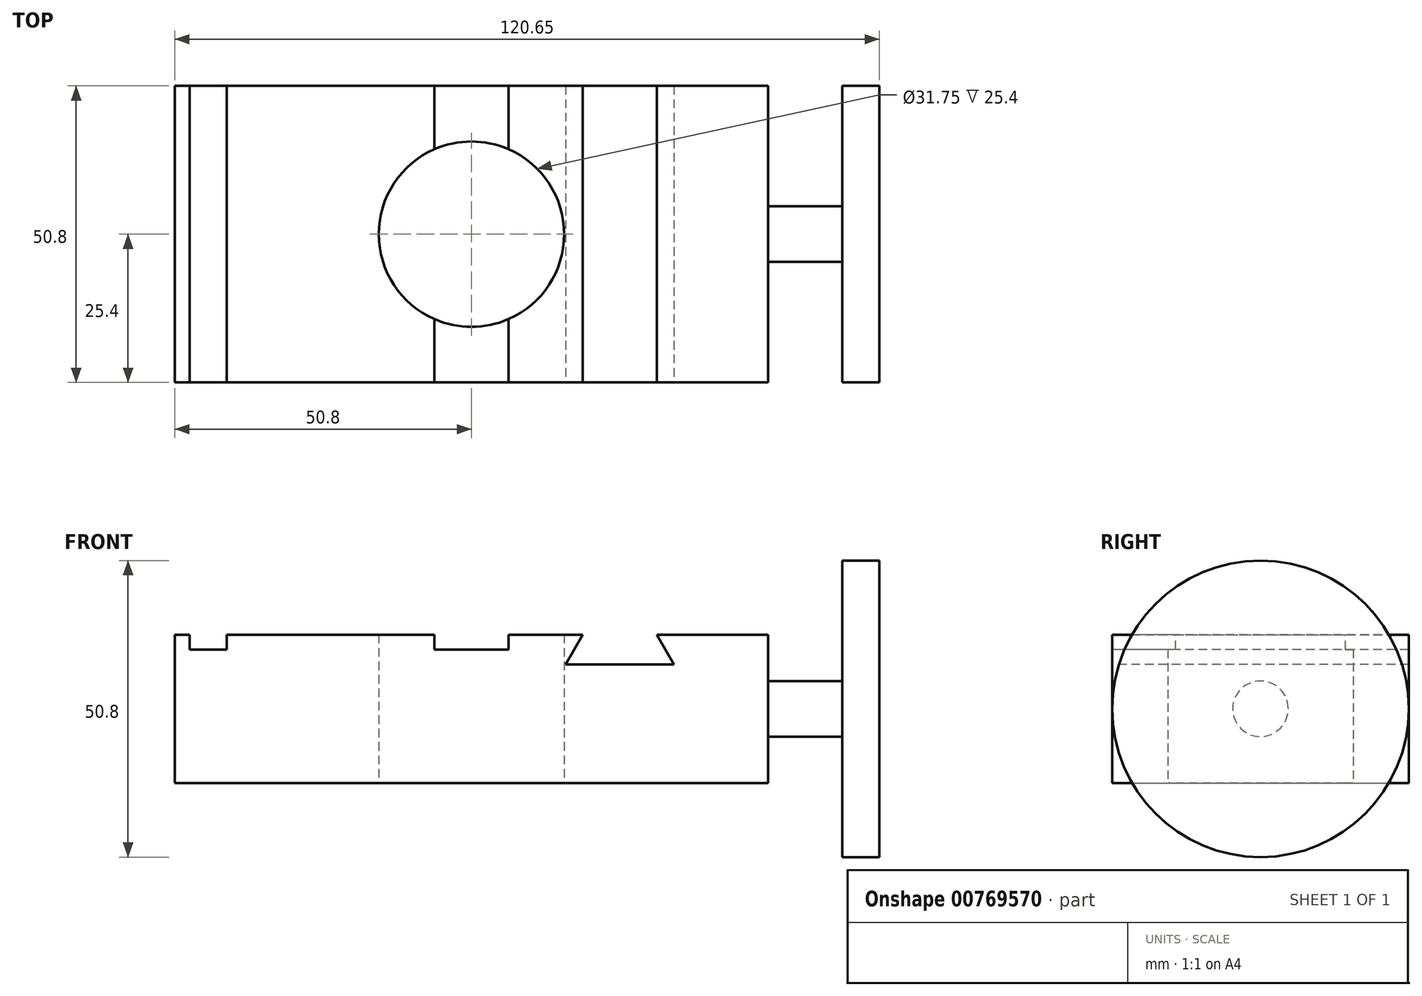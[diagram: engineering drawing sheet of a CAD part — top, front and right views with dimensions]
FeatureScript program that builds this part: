
annotation { "Feature Type Name" : "Feature", "Feature Type Description" : "" }
export const myFeature = defineFeature(function(context is Context, id is Id, definition is map)
    precondition{}
    {
        {
            var Q0;
            Q0=qCreatedBy(makeId("Top.planeOp"),FACE);
            var sketch = newSketch(context, id + "F0", { "sketchPlane" : qUnion([Q0])});
            skLineSegment(sketch, "E0.bottom", {"start": v(50.8, -25.4) * mm, "end": v(-50.8, -25.4) * mm});
            skLineSegment(sketch, "E0.top", {"start": v(50.8, 25.4) * mm, "end": v(-50.8, 25.4) * mm});
            skLineSegment(sketch, "E0.left", {"start": v(50.8, -25.4) * mm, "end": v(50.8, 25.4) * mm});
            skLineSegment(sketch, "E0.right", {"start": v(-50.8, -25.4) * mm, "end": v(-50.8, 25.4) * mm});
            skPoint(sketch, "E0.middle", {"position": v(0, 0) * mm});
            skCircle(sketch, "E1", {"center": v(0, 0) * mm, "radius": 15.88 * mm});
            skSolve(sketch);
        }
        {
            var Q0;
            Q0=makeQuery(id+"F0.imprint","IMPRINT",FACE,{"disambiguationData":[TD([[makeQuery(id+"F0.imprint","IMPRINT",EDGE,{"derivedFrom":sQuery(id+"F0.wireOp",EDGE,"E0.bottom")}),-1.0]])]});
            extrude(context, id + "F1", {"entities" : qUnion([Q0]), "depth" : 25.4 * mm, "offsetDistance" : 25.4 * mm});
        }
        {
            var Q0;
            Q0=makeQuery(id+"F1.opExtrude","CAP_FACE",FACE,{"disambiguationData":[OSD([sQuery(id+"F0.wireOp",EDGE,"E0.bottom"),sQuery(id+"F0.wireOp",EDGE,"E0.top"),sQuery(id+"F0.wireOp",EDGE,"E0.left"),sQuery(id+"F0.wireOp",EDGE,"E0.right"),sQuery(id+"F0.wireOp",EDGE,"E1")])],"isStart":false});
            var sketch = newSketch(context, id + "F2", { "sketchPlane" : qUnion([Q0])});
            skLineSegment(sketch, "E2.bottom", {"start": v(-48.26, 25.4) * mm, "end": v(-41.9, 25.4) * mm});
            skLineSegment(sketch, "E2.top", {"start": v(-48.26, -25.4) * mm, "end": v(-41.9, -25.4) * mm});
            skLineSegment(sketch, "E2.left", {"start": v(-48.26, 25.4) * mm, "end": v(-48.26, -25.4) * mm});
            skLineSegment(sketch, "E2.right", {"start": v(-41.9, 25.4) * mm, "end": v(-41.9, -25.4) * mm});
            skLineSegment(sketch, "E3", {"start": v(-6.35, 25.4) * mm, "end": v(-6.35, -25.4) * mm});
            skLineSegment(sketch, "E4", {"start": v(-6.35, -25.4) * mm, "end": v(6.35, -25.4) * mm});
            skLineSegment(sketch, "E5", {"start": v(6.35, -25.4) * mm, "end": v(6.35, 25.4) * mm});
            skLineSegment(sketch, "E6", {"start": v(6.35, 25.4) * mm, "end": v(-6.35, 25.4) * mm});
            skPoint(sketch, "E7", {"position": v(0, 0) * mm});
            skLineSegment(sketch, "E8", {"start": v(0, 25.4) * mm, "end": v(0, -25.4) * mm, "construction": true});
            skSolve(sketch);
        }
        {
            var Q0;
            {var subQ0=sQuery(id+"F2.wireOp",EDGE,"E6");Q0=makeQuery(id+"F2.imprint","IMPRINT",FACE,{"disambiguationData":[TD([[makeQuery(id+"F2.imprint","IMPRINT",EDGE,{"derivedFrom":subQ0}),1.0]])]});}
            var Q1;
            {var subQ0=sQuery(id+"F2.wireOp",EDGE,"E4");Q1=makeQuery(id+"F2.imprint","IMPRINT",FACE,{"disambiguationData":[TD([[makeQuery(id+"F2.imprint","IMPRINT",EDGE,{"derivedFrom":subQ0}),-1.0]])]});}
            var Q2;
            Q2=makeQuery(id+"F2.imprint","IMPRINT",FACE,{"disambiguationData":[TD([[makeQuery(id+"F2.imprint","IMPRINT",EDGE,{"derivedFrom":sQuery(id+"F2.wireOp",EDGE,"E2.bottom")}),1.0]])]});
            extrude(context, id + "F3", {"entities" : qUnion([Q0, Q1, Q2]), "operationType" : NewBodyOperationType.REMOVE, "oppositeDirection" : true, "depth" : 2.54 * mm, "offsetDistance" : 25.4 * mm});
        }
        {
            var Q0;
            Q0=makeQuery(id+"F1.opExtrude","SWEPT_FACE",FACE,{"disambiguationData":[OSD([sQuery(id+"F0.wireOp",EDGE,"E0.bottom")])]});
            var sketch = newSketch(context, id + "F4", { "sketchPlane" : qUnion([Q0])});
            skLineSegment(sketch, "E9", {"start": v(19.05, 25.4) * mm, "end": v(16.12, 20.32) * mm});
            skLineSegment(sketch, "E10", {"start": v(16.12, 20.32) * mm, "end": v(34.68, 20.32) * mm});
            skLineSegment(sketch, "E11", {"start": v(34.68, 20.32) * mm, "end": v(31.75, 25.4) * mm});
            skLineSegment(sketch, "E12", {"start": v(31.75, 25.4) * mm, "end": v(19.05, 25.4) * mm});
            skLineSegment(sketch, "E13", {"start": v(25.4, 25.4) * mm, "end": v(25.4, 20.32) * mm, "construction": true});
            skSolve(sketch);
        }
        {
            var Q0;
            Q0=makeQuery(id+"F4.imprint","IMPRINT",FACE,{"disambiguationData":[TD([[makeQuery(id+"F4.imprint","IMPRINT",EDGE,{"derivedFrom":sQuery(id+"F4.wireOp",EDGE,"E9")}),1.0]])]});
            extrude(context, id + "F5", {"entities" : qUnion([Q0]), "operationType" : NewBodyOperationType.REMOVE, "endBound" : BoundingType.THROUGH_ALL, "oppositeDirection" : true, "depth" : 25.4 * mm, "offsetDistance" : 25.4 * mm});
        }
        {
            var Q0;
            Q0=makeQuery(id+"F1.opExtrude","SWEPT_FACE",FACE,{"disambiguationData":[OSD([sQuery(id+"F0.wireOp",EDGE,"E0.left")])]});
            var sketch = newSketch(context, id + "F6", { "sketchPlane" : qUnion([Q0])});
            skCircle(sketch, "E14", {"center": v(0, 12.7) * mm, "radius": 4.76 * mm});
            skPoint(sketch, "E14.centerSnap0", {"position": v(-25.4, 12.7) * mm});
            skPoint(sketch, "E14.centerSnap1", {"position": v(0, 25.4) * mm});
            skSolve(sketch);
        }
        {
            var Q0;
            Q0=makeQuery(id+"F6.imprint","IMPRINT",FACE,{"disambiguationData":[TD([[makeQuery(id+"F6.imprint","IMPRINT",EDGE,{"derivedFrom":sQuery(id+"F6.wireOp",EDGE,"E14")}),1.0]])]});
            extrude(context, id + "F7", {"entities" : qUnion([Q0]), "operationType" : NewBodyOperationType.ADD, "depth" : 12.7 * mm, "offsetDistance" : 25.4 * mm});
        }
        {
            var Q0;
            Q0=makeQuery(id+"F7.opExtrude","CAP_FACE",FACE,{"disambiguationData":[OSD([sQuery(id+"F6.wireOp",EDGE,"E14")])],"isStart":false});
            var sketch = newSketch(context, id + "F8", { "sketchPlane" : qUnion([Q0])});
            skCircle(sketch, "E15", {"center": v(0, 12.7) * mm, "radius": 25.4 * mm});
            skSolve(sketch);
        }
        {
            var Q0;
            Q0=makeQuery(id+"F8.imprint","IMPRINT",FACE,{"disambiguationData":[TD([[makeQuery(id+"F8.imprint","IMPRINT",EDGE,{"derivedFrom":makeQuery(id+"F7.opExtrude","CAP_EDGE",EDGE,{"disambiguationData":[OSD([sQuery(id+"F6.wireOp",EDGE,"E14")])],"isStart":false})}),1.0]])]});
            var Q1;
            Q1=makeQuery(id+"F8.imprint","IMPRINT",FACE,{"disambiguationData":[TD([[makeQuery(id+"F8.imprint","IMPRINT",EDGE,{"derivedFrom":sQuery(id+"F8.wireOp",EDGE,"E15")}),1.0]])]});
            extrude(context, id + "F9", {"entities" : qUnion([Q0, Q1]), "operationType" : NewBodyOperationType.ADD, "depth" : 6.35 * mm, "offsetDistance" : 25.4 * mm});
        }
    });
